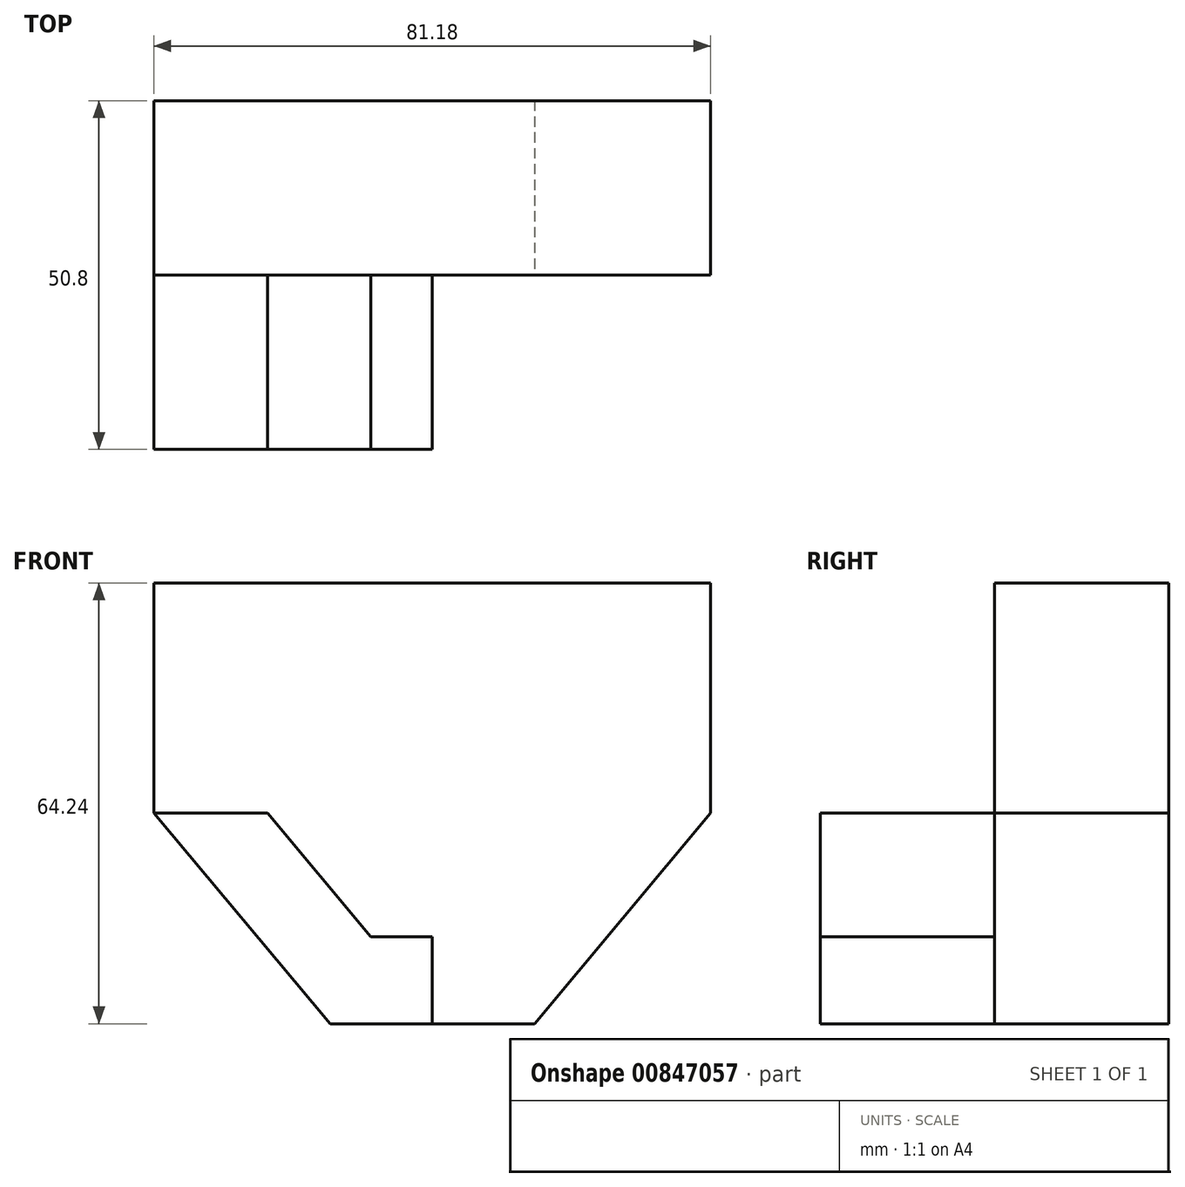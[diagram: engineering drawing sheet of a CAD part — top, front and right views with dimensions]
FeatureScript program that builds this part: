
annotation { "Feature Type Name" : "Feature", "Feature Type Description" : "" }
export const myFeature = defineFeature(function(context is Context, id is Id, definition is map)
    precondition{}
    {
        {
            var Q0;
            Q0=qCreatedBy(makeId("Front.planeOp"),FACE);
            var sketch = newSketch(context, id + "F0", { "sketchPlane" : qUnion([Q0])});
            skLineSegment(sketch, "E0.bottom", {"start": v(-24.45, 14.14) * mm, "end": v(56.73, 14.14) * mm});
            skLineSegment(sketch, "E0.top", {"start": v(-24.45, -19.4) * mm, "end": v(-7.89, -19.4) * mm});
            skLineSegment(sketch, "E0.left", {"start": v(-24.45, 14.14) * mm, "end": v(-24.45, -19.4) * mm});
            skLineSegment(sketch, "E0.right", {"start": v(56.73, 14.14) * mm, "end": v(56.73, -19.4) * mm});
            skLineSegment(sketch, "E1", {"start": v(-24.45, -19.4) * mm, "end": v(1.25, -50.1) * mm});
            skLineSegment(sketch, "E2", {"start": v(1.25, -50.1) * mm, "end": v(31.02, -50.1) * mm});
            skLineSegment(sketch, "E3", {"start": v(31.02, -50.1) * mm, "end": v(56.73, -19.4) * mm});
            skLineSegment(sketch, "E4", {"start": v(16.14, -50.1) * mm, "end": v(16.14, -37.4) * mm});
            skLineSegment(sketch, "E5.0", {"start": v(-7.89, -19.4) * mm, "end": v(7.18, -37.4) * mm});
            skLineSegment(sketch, "E6.0", {"start": v(7.18, -37.4) * mm, "end": v(25.1, -37.4) * mm});
            skLineSegment(sketch, "E7.0", {"start": v(25.1, -37.4) * mm, "end": v(40.16, -19.4) * mm});
            skLineSegment(sketch, "E8.trimOffspring", {"start": v(40.16, -19.4) * mm, "end": v(56.73, -19.4) * mm});
            skPoint(sketch, "E9.orphan", {"position": v(16.14, -19.4) * mm});
            skSolve(sketch);
        }
        {
            var Q0;
            Q0=makeQuery(id+"F0.imprint","IMPRINT",FACE,{"disambiguationData":[TD([[makeQuery(id+"F0.imprint","IMPRINT",EDGE,{"derivedFrom":sQuery(id+"F0.wireOp",EDGE,"E0.top")}),-1.0]])]});
            extrude(context, id + "F1", {"entities" : qUnion([Q0]), "depth" : 25.4 * mm, "offsetDistance" : 25.4 * mm});
        }
        {
            var Q0;
            Q0 = qSketchRegion(id + "F0", true);
            extrude(context, id + "F2", {"entities" : qUnion([Q0]), "operationType" : NewBodyOperationType.ADD, "oppositeDirection" : true, "depth" : 25.4 * mm, "offsetDistance" : 25.4 * mm});
        }
    });
